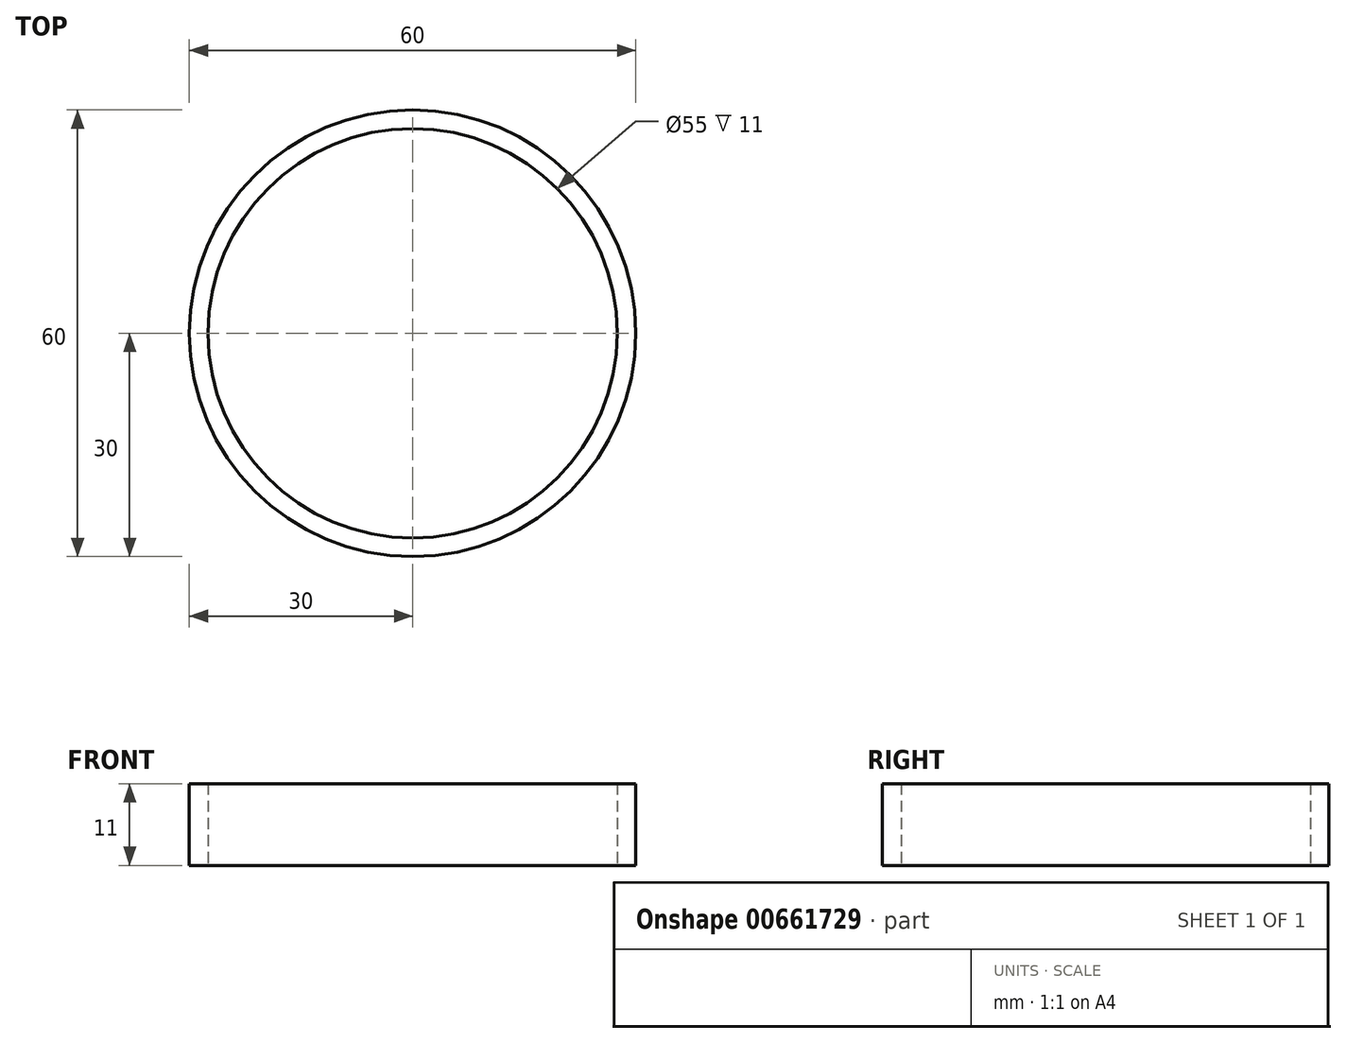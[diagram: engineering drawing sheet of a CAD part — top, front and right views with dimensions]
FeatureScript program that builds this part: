
annotation { "Feature Type Name" : "Feature", "Feature Type Description" : "" }
export const myFeature = defineFeature(function(context is Context, id is Id, definition is map)
    precondition{}
    {
        {
            var Q0;
            Q0=qCreatedBy(makeId("Top.planeOp"),FACE);
            var sketch = newSketch(context, id + "F0", { "sketchPlane" : qUnion([Q0])});
            skCircle(sketch, "E0", {"center": v(0, 0) * mm, "radius": 30 * mm});
            skCircle(sketch, "E1", {"center": v(0, 0) * mm, "radius": 27.5 * mm});
            skSolve(sketch);
        }
        {
            var Q0;
            Q0 = qSketchRegion(id + "F0", true);
            extrude(context, id + "F1", {"entities" : qUnion([Q0]), "endBound" : BoundingType.SYMMETRIC, "depth" : 11 * mm, "offsetDistance" : 25 * mm});
        }
    });
